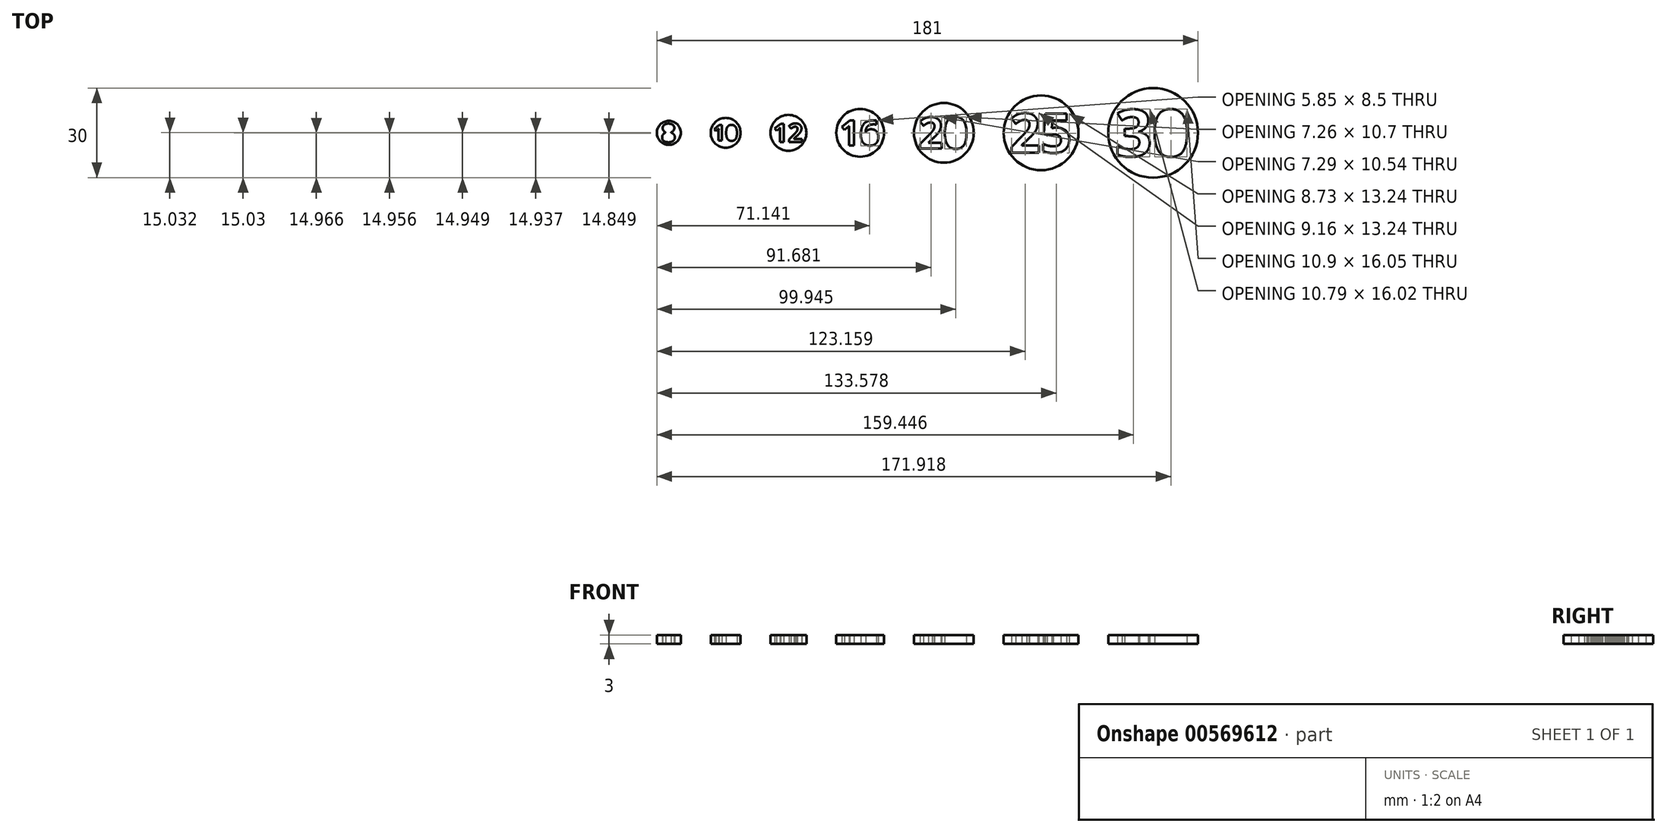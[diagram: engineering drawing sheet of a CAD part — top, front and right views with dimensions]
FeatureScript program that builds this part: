
annotation { "Feature Type Name" : "Feature", "Feature Type Description" : "" }
export const myFeature = defineFeature(function(context is Context, id is Id, definition is map)
    precondition{}
    {
        {
            var Q0;
            Q0=qCreatedBy(makeId("Top.planeOp"),FACE);
            var sketch = newSketch(context, id + "F0", { "sketchPlane" : qUnion([Q0])});
            skCircle(sketch, "E0", {"center": v(-70, 0) * mm, "radius": 10 * mm});
            skCircle(sketch, "E1", {"center": v(-37.5, 0) * mm, "radius": 12.5 * mm});
            skCircle(sketch, "E2", {"center": v(0, 0) * mm, "radius": 15 * mm});
            skCircle(sketch, "E3", {"center": v(-98, 0) * mm, "radius": 8 * mm});
            skCircle(sketch, "E4", {"center": v(-122, 0) * mm, "radius": 6 * mm});
            skCircle(sketch, "E5", {"center": v(-143, 0) * mm, "radius": 5 * mm});
            skCircle(sketch, "E6", {"center": v(-162, 0) * mm, "radius": 4 * mm});
            skText(sketch, "E7", { "text": "8", "fontName": "OpenSans-Bold.ttf"});
            skText(sketch, "E8", { "text": "10\n", "fontName": "OpenSans-Bold.ttf"});
            skText(sketch, "E9", { "text": "12", "fontName": "OpenSans-Bold.ttf"});
            skText(sketch, "E10", { "text": "16\n", "fontName": "OpenSans-Bold.ttf"});
            skText(sketch, "E11", { "text": "20", "fontName": "OpenSans-Bold.ttf"});
            skText(sketch, "E12", { "text": "25\n", "fontName": "OpenSans-Bold.ttf"});
            skText(sketch, "E13", { "text": "30", "fontName": "OpenSans-Bold.ttf"});
            const initialGuessF0  = {"E7": [-0.16456, -0.00307, 1, 0, 0.00614], "E8": [-0.14726, -0.00262, 1, 0, 0.00524], "E9": [-0.12712, -0.00314, 1, 0, 0.00627], "E10": [-0.10482, -0.00418, 1, 0, 0.00836], "E11": [-0.07852, -0.00524, 1, 0, 0.01048], "E12": [-0.04812, -0.00659, 1, 0, 0.01317], "E13": [-0.01278, -0.00786, 1, 0, 0.01572]};
            skSetInitialGuess(sketch, initialGuessF0);
            skSolve(sketch);
        }
        {
            var Q0;
            Q0=makeQuery(id+"F0.imprint","IMPRINT",FACE,{"disambiguationData":[TD([[makeQuery(id+"F0.imprint","IMPRINT",EDGE,{"derivedFrom":sQuery(id+"F0.wireOp",EDGE,"E6")}),1.0]])]});
            var Q1;
            Q1=makeQuery(id+"F0.imprint","IMPRINT",FACE,{"disambiguationData":[TD([[makeQuery(id+"F0.imprint","IMPRINT",EDGE,{"derivedFrom":sQuery(id+"F0.wireOp",EDGE,"E5")}),1.0]])]});
            var Q2;
            Q2=makeQuery(id+"F0.imprint","IMPRINT",FACE,{"disambiguationData":[TD([[makeQuery(id+"F0.imprint","IMPRINT",EDGE,{"derivedFrom":sQuery(id+"F0.wireOp",EDGE,"E4")}),1.0]])]});
            var Q3;
            Q3=makeQuery(id+"F0.imprint","IMPRINT",FACE,{"disambiguationData":[TD([[makeQuery(id+"F0.imprint","IMPRINT",EDGE,{"derivedFrom":sQuery(id+"F0.wireOp",EDGE,"E3")}),1.0]])]});
            var Q4;
            Q4=makeQuery(id+"F0.imprint","IMPRINT",FACE,{"disambiguationData":[TD([[makeQuery(id+"F0.imprint","IMPRINT",EDGE,{"derivedFrom":sQuery(id+"F0.wireOp",EDGE,"E0")}),1.0]])]});
            var Q5;
            Q5=makeQuery(id+"F0.imprint","IMPRINT",FACE,{"disambiguationData":[TD([[makeQuery(id+"F0.imprint","IMPRINT",EDGE,{"derivedFrom":sQuery(id+"F0.wireOp",EDGE,"E2")}),1.0]])]});
            var Q6;
            Q6=makeQuery(id+"F0.imprint","IMPRINT",FACE,{"disambiguationData":[TD([[makeQuery(id+"F0.imprint","IMPRINT",EDGE,{"derivedFrom":sQuery(id+"F0.wireOp",EDGE,"E1")}),1.0]])]});
            extrude(context, id + "F1", {"entities" : qUnion([Q0, Q1, Q2, Q3, Q4, Q5, Q6]), "depth" : 3 * mm, "offsetDistance" : 25 * mm});
        }
    });
